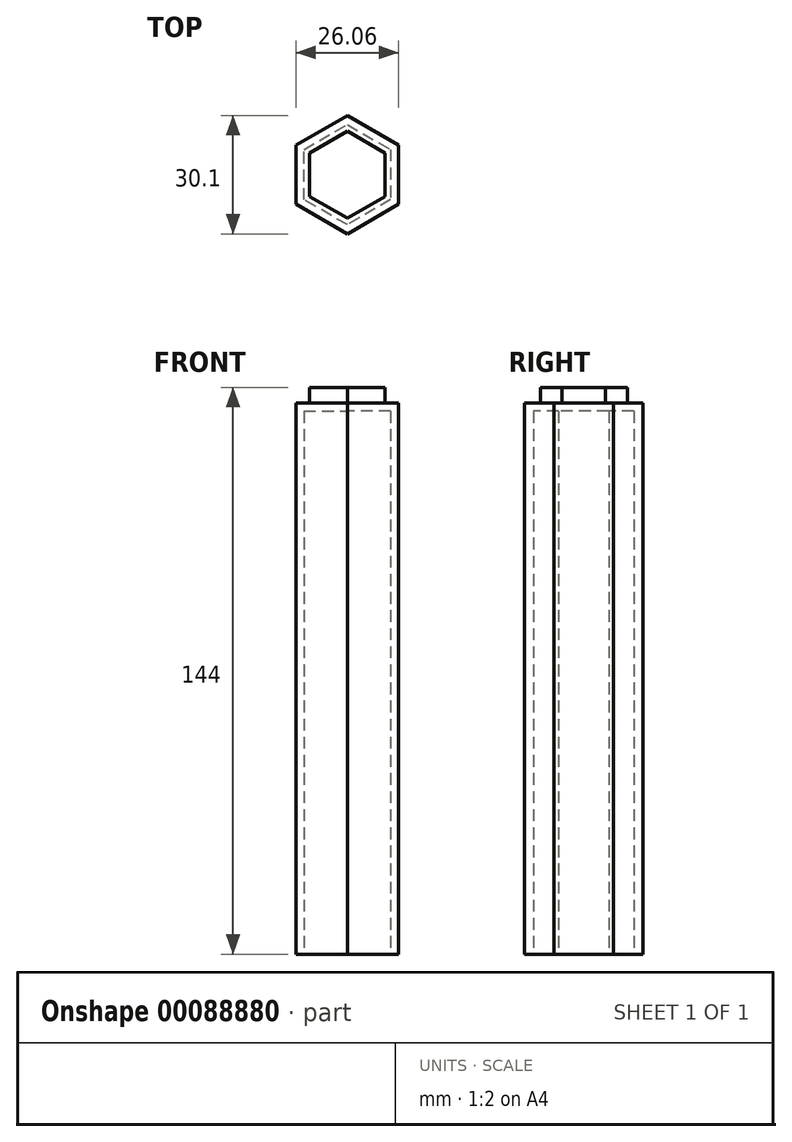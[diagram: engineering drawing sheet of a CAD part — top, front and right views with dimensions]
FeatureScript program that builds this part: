
annotation { "Feature Type Name" : "Feature", "Feature Type Description" : "" }
export const myFeature = defineFeature(function(context is Context, id is Id, definition is map)
    precondition{}
    {
        {
            var Q0;
            Q0=qCreatedBy(makeId("Top.planeOp"),FACE);
            var sketch = newSketch(context, id + "F0", { "sketchPlane" : qUnion([Q0])});
            skCircle(sketch, "E0.cCircle", {"center": v(0, 0) * mm, "radius": 15.05 * mm, "construction": true});
            skLineSegment(sketch, "E0.0", {"start": v(13.03, -7.52) * mm, "end": v(0, -15.05) * mm});
            skLineSegment(sketch, "E0.1", {"start": v(0, -15.05) * mm, "end": v(-13.03, -7.52) * mm});
            skLineSegment(sketch, "E0.2", {"start": v(-13.03, -7.52) * mm, "end": v(-13.03, 7.52) * mm});
            skLineSegment(sketch, "E0.3", {"start": v(-13.03, 7.52) * mm, "end": v(0, 15.05) * mm});
            skLineSegment(sketch, "E0.4", {"start": v(0, 15.05) * mm, "end": v(13.03, 7.52) * mm});
            skLineSegment(sketch, "E0.5", {"start": v(13.03, 7.52) * mm, "end": v(13.03, -7.52) * mm});
            skSolve(sketch);
        }
        {
            var Q0;
            Q0 = qSketchRegion(id + "F0", true);
            extrude(context, id + "F1", {"entities" : qUnion([Q0]), "depth" : 140 * mm});
        }
        {
            var Q0;
            Q0=makeQuery(id+"F1.opExtrude","CAP_FACE",FACE,{"disambiguationData":[OSD([sQuery(id+"F0.wireOp",EDGE,"E0.0"),sQuery(id+"F0.wireOp",EDGE,"E0.1"),sQuery(id+"F0.wireOp",EDGE,"E0.2"),sQuery(id+"F0.wireOp",EDGE,"E0.3"),sQuery(id+"F0.wireOp",EDGE,"E0.4"),sQuery(id+"F0.wireOp",EDGE,"E0.5")])],"isStart":true});
            shell(context, id + "F2", {"entities" : qUnion([Q0]), "thickness" : 2 * mm});
        }
        {
            var Q0;
            Q0=makeQuery(id+"F1.opExtrude","CAP_FACE",FACE,{"disambiguationData":[OSD([sQuery(id+"F0.wireOp",EDGE,"E0.0"),sQuery(id+"F0.wireOp",EDGE,"E0.1"),sQuery(id+"F0.wireOp",EDGE,"E0.2"),sQuery(id+"F0.wireOp",EDGE,"E0.3"),sQuery(id+"F0.wireOp",EDGE,"E0.4"),sQuery(id+"F0.wireOp",EDGE,"E0.5")])],"isStart":false});
            var sketch = newSketch(context, id + "F3", { "sketchPlane" : qUnion([Q0])});
            skCircle(sketch, "E1.cCircle", {"center": v(0, 0) * mm, "radius": 11.05 * mm, "construction": true});
            skLineSegment(sketch, "E1.0", {"start": v(9.57, -5.52) * mm, "end": v(0, -11.05) * mm});
            skLineSegment(sketch, "E1.1", {"start": v(0, -11.05) * mm, "end": v(-9.57, -5.52) * mm});
            skLineSegment(sketch, "E1.2", {"start": v(-9.57, -5.52) * mm, "end": v(-9.57, 5.52) * mm});
            skLineSegment(sketch, "E1.3", {"start": v(-9.57, 5.52) * mm, "end": v(0, 11.05) * mm});
            skLineSegment(sketch, "E1.4", {"start": v(0, 11.05) * mm, "end": v(9.57, 5.52) * mm});
            skLineSegment(sketch, "E1.5", {"start": v(9.57, 5.52) * mm, "end": v(9.57, -5.52) * mm});
            skSolve(sketch);
        }
        {
            var Q0;
            Q0 = qSketchRegion(id + "F3", true);
            extrude(context, id + "F4", {"entities" : qUnion([Q0]), "operationType" : NewBodyOperationType.ADD, "depth" : 4 * mm});
        }
    });
